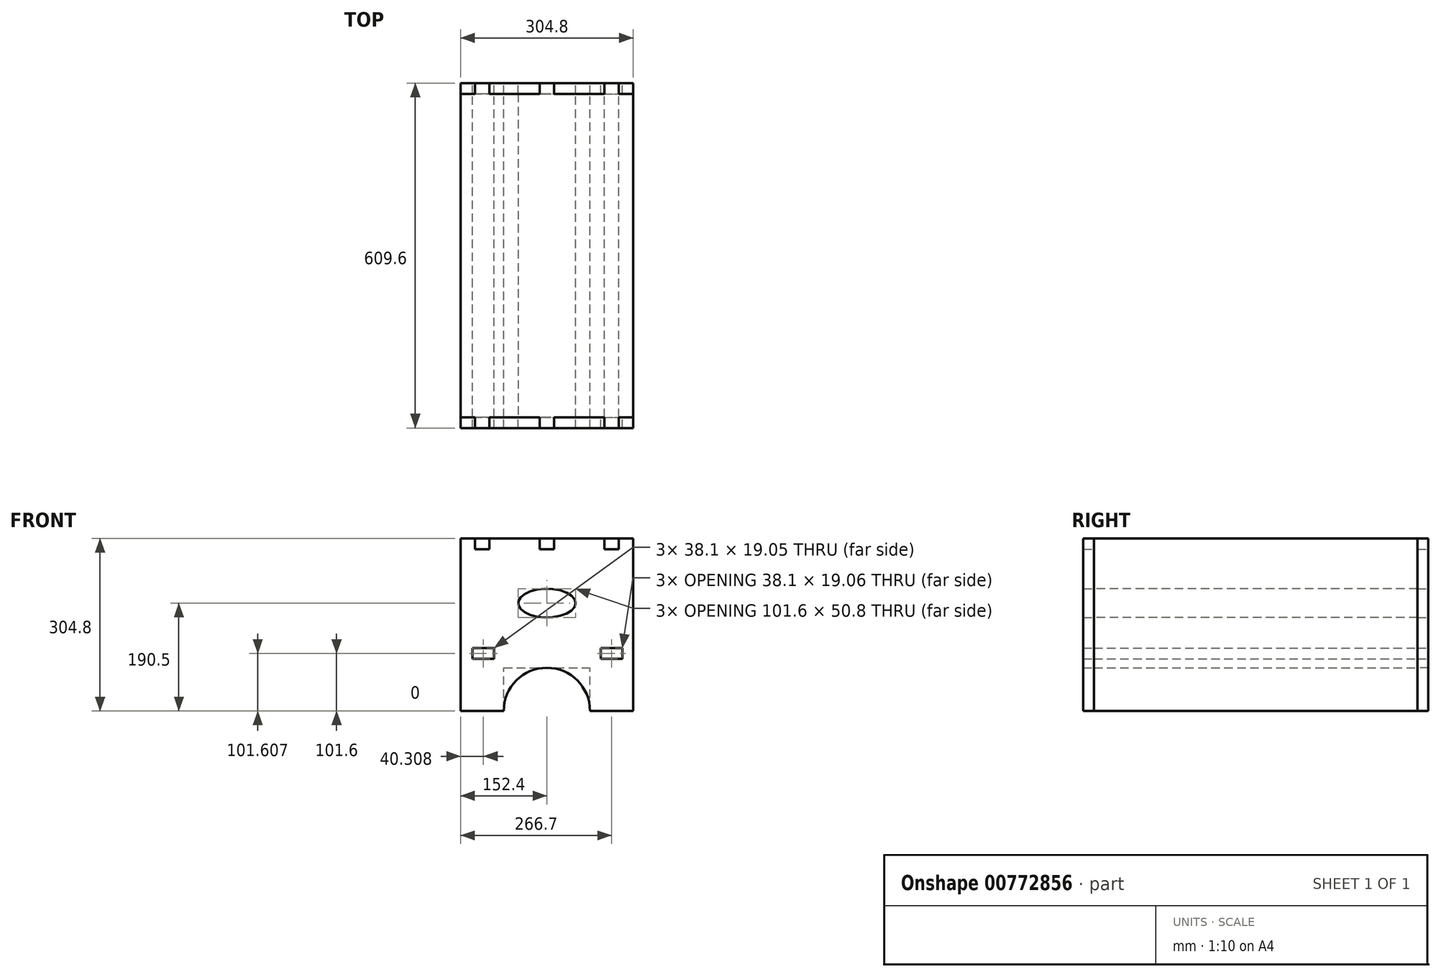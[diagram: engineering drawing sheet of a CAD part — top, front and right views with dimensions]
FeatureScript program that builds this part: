
annotation { "Feature Type Name" : "Feature", "Feature Type Description" : "" }
export const myFeature = defineFeature(function(context is Context, id is Id, definition is map)
    precondition{}
    {
        {
            var Q0;
            Q0=qCreatedBy(makeId("Front.planeOp"),FACE);
            var sketch = newSketch(context, id + "F0", { "sketchPlane" : qUnion([Q0])});
            skLineSegment(sketch, "E0.bottom", {"start": v(0, 0) * mm, "end": v(304.8, 0) * mm});
            skLineSegment(sketch, "E0.left", {"start": v(0, 0) * mm, "end": v(0, 304.8) * mm});
            skLineSegment(sketch, "E0.right", {"start": v(304.8, 0) * mm, "end": v(304.8, 304.8) * mm});
            skLineSegment(sketch, "E1", {"start": v(0, 0) * mm, "end": v(76.2, 0) * mm});
            skLineSegment(sketch, "E2", {"start": v(304.8, 0) * mm, "end": v(228.6, 0) * mm});
            skLineSegment(sketch, "E3", {"start": v(228.6, 0) * mm, "end": v(228.6, 76.2) * mm});
            skLineSegment(sketch, "E4", {"start": v(76.2, 0) * mm, "end": v(76.2, 76.2) * mm});
            skLineSegment(sketch, "E5", {"start": v(76.2, 76.2) * mm, "end": v(228.6, 76.2) * mm});
            skEllipse(sketch, "E6", {"center": v(152.4, 190.5) * mm, "majorRadius": 50.8 * mm, "minorRadius": 25.4 * mm, "majorAxis": v(1, 0)});
            skLineSegment(sketch, "E7.bottom", {"start": v(254, 111.13) * mm, "end": v(279.4, 111.13) * mm});
            skLineSegment(sketch, "E7.top", {"start": v(254, 92.07) * mm, "end": v(279.4, 92.07) * mm});
            skLineSegment(sketch, "E8", {"start": v(279.4, 111.13) * mm, "end": v(279.4, 92.07) * mm});
            skLineSegment(sketch, "E9", {"start": v(254, 111.13) * mm, "end": v(254, 92.07) * mm});
            skLineSegment(sketch, "E10.top", {"start": v(53, 92.08) * mm, "end": v(25.4, 92.08) * mm});
            skLineSegment(sketch, "E11.top", {"start": v(139.7, 285.75) * mm, "end": v(165.1, 285.75) * mm});
            skLineSegment(sketch, "E11.left", {"start": v(139.7, 304.8) * mm, "end": v(139.7, 285.75) * mm});
            skLineSegment(sketch, "E11.right", {"start": v(165.1, 304.8) * mm, "end": v(165.1, 285.75) * mm});
            skLineSegment(sketch, "E12", {"start": v(0, 304.8) * mm, "end": v(304.8, 304.8) * mm});
            skLineSegment(sketch, "E13", {"start": v(254, 304.8) * mm, "end": v(254, 285.75) * mm});
            skLineSegment(sketch, "E14", {"start": v(254, 285.75) * mm, "end": v(279.4, 285.75) * mm});
            skLineSegment(sketch, "E15", {"start": v(50.8, 304.8) * mm, "end": v(50.8, 285.75) * mm});
            skLineSegment(sketch, "E16", {"start": v(50.8, 285.75) * mm, "end": v(25.4, 285.75) * mm});
            skLineSegment(sketch, "E17", {"start": v(279.4, 285.75) * mm, "end": v(279.4, 304.8) * mm});
            skLineSegment(sketch, "E18", {"start": v(25.4, 285.75) * mm, "end": v(25.4, 304.8) * mm});
            skLineSegment(sketch, "E19.bottom", {"start": v(27.6, 111.13) * mm, "end": v(53, 111.13) * mm});
            skLineSegment(sketch, "E19.left", {"start": v(27.6, 111.13) * mm, "end": v(27.6, 92.08) * mm});
            skLineSegment(sketch, "E19.right", {"start": v(53, 111.13) * mm, "end": v(53, 92.08) * mm});
            skLineSegment(sketch, "E20", {"start": v(53, 92.08) * mm, "end": v(59.36, 92.08) * mm});
            skLineSegment(sketch, "E21.bottom", {"start": v(59.36, 92.08) * mm, "end": v(21.26, 92.08) * mm});
            skLineSegment(sketch, "E21.top", {"start": v(59.36, 111.13) * mm, "end": v(21.26, 111.13) * mm});
            skLineSegment(sketch, "E21.left", {"start": v(59.36, 92.08) * mm, "end": v(59.36, 111.13) * mm});
            skLineSegment(sketch, "E21.right", {"start": v(21.26, 92.08) * mm, "end": v(21.26, 111.13) * mm});
            skLineSegment(sketch, "E22", {"start": v(254, 92.07) * mm, "end": v(247.65, 92.07) * mm});
            skLineSegment(sketch, "E23.bottom", {"start": v(247.65, 92.07) * mm, "end": v(285.75, 92.07) * mm});
            skLineSegment(sketch, "E23.top", {"start": v(247.65, 111.12) * mm, "end": v(285.75, 111.12) * mm});
            skLineSegment(sketch, "E23.left", {"start": v(247.65, 92.07) * mm, "end": v(247.65, 111.12) * mm});
            skLineSegment(sketch, "E23.right", {"start": v(285.75, 92.07) * mm, "end": v(285.75, 111.12) * mm});
            skSolve(sketch);
        }
        {
            var Q0;
            {var subQ7=sQuery(id+"F0.wireOp",EDGE,"E0.left");Q0=makeQuery(id+"F0.imprint","IMPRINT",FACE,{"disambiguationData":[TD([[makeQuery(id+"F0.imprint","IMPRINT",EDGE,{"derivedFrom":subQ7}),-1.0]])]});}
            extrude(context, id + "F1", {"entities" : qUnion([Q0]), "depth" : 19.05 * mm, "offsetDistance" : 25.4 * mm});
        }
        {
            var Q0;
            Q0=makeQuery(id+"F1.opExtrude","CAP_FACE",FACE,{"disambiguationData":[OSD([sQuery(id+"F0.wireOp",EDGE,"E0.left"),sQuery(id+"F0.wireOp",EDGE,"E0.right"),sQuery(id+"F0.wireOp",EDGE,"E1"),sQuery(id+"F0.wireOp",EDGE,"E2"),sQuery(id+"F0.wireOp",EDGE,"E3"),sQuery(id+"F0.wireOp",EDGE,"E4"),sQuery(id+"F0.wireOp",EDGE,"E5"),sQuery(id+"F0.wireOp",EDGE,"E6"),sQuery(id+"F0.wireOp",EDGE,"E7.bottom"),sQuery(id+"F0.wireOp",EDGE,"E8"),sQuery(id+"F0.wireOp",EDGE,"E9"),sQuery(id+"F0.wireOp",EDGE,"E11.top"),sQuery(id+"F0.wireOp",EDGE,"E11.left"),sQuery(id+"F0.wireOp",EDGE,"E11.right"),sQuery(id+"F0.wireOp",EDGE,"E12"),sQuery(id+"F0.wireOp",EDGE,"E13"),sQuery(id+"F0.wireOp",EDGE,"E14"),sQuery(id+"F0.wireOp",EDGE,"E15"),sQuery(id+"F0.wireOp",EDGE,"E16"),sQuery(id+"F0.wireOp",EDGE,"E17"),sQuery(id+"F0.wireOp",EDGE,"E18"),sQuery(id+"F0.wireOp",EDGE,"E21.bottom"),sQuery(id+"F0.wireOp",EDGE,"E21.top"),sQuery(id+"F0.wireOp",EDGE,"E21.left"),sQuery(id+"F0.wireOp",EDGE,"E21.right"),sQuery(id+"F0.wireOp",EDGE,"E23.bottom"),sQuery(id+"F0.wireOp",EDGE,"E23.top"),sQuery(id+"F0.wireOp",EDGE,"E23.left"),sQuery(id+"F0.wireOp",EDGE,"E23.right")])],"isStart":true});
            var sketch = newSketch(context, id + "F2", { "sketchPlane" : qUnion([Q0])});
            skLineSegment(sketch, "E24.bottom", {"start": v(-247.65, 111.12) * mm, "end": v(-285.75, 111.12) * mm});
            skLineSegment(sketch, "E24.top", {"start": v(-247.65, 92.07) * mm, "end": v(-285.75, 92.07) * mm});
            skLineSegment(sketch, "E24.left", {"start": v(-247.65, 111.12) * mm, "end": v(-247.65, 92.07) * mm});
            skLineSegment(sketch, "E24.right", {"start": v(-285.75, 111.12) * mm, "end": v(-285.75, 92.07) * mm});
            skLineSegment(sketch, "E25.bottom", {"start": v(-59.36, 92.08) * mm, "end": v(-21.26, 92.08) * mm});
            skLineSegment(sketch, "E25.top", {"start": v(-59.36, 111.13) * mm, "end": v(-21.26, 111.13) * mm});
            skLineSegment(sketch, "E25.left", {"start": v(-59.36, 92.08) * mm, "end": v(-59.36, 111.13) * mm});
            skLineSegment(sketch, "E25.right", {"start": v(-21.26, 92.08) * mm, "end": v(-21.26, 111.13) * mm});
            skLineSegment(sketch, "E26.bottom", {"start": v(-25.4, 285.75) * mm, "end": v(-50.8, 285.75) * mm});
            skLineSegment(sketch, "E26.top", {"start": v(-25.4, 304.8) * mm, "end": v(-50.8, 304.8) * mm});
            skLineSegment(sketch, "E26.left", {"start": v(-25.4, 285.75) * mm, "end": v(-25.4, 304.8) * mm});
            skLineSegment(sketch, "E26.right", {"start": v(-50.8, 285.75) * mm, "end": v(-50.8, 304.8) * mm});
            skLineSegment(sketch, "E27.bottom", {"start": v(-139.7, 285.75) * mm, "end": v(-165.1, 285.75) * mm});
            skLineSegment(sketch, "E27.top", {"start": v(-139.7, 304.8) * mm, "end": v(-165.1, 304.8) * mm});
            skLineSegment(sketch, "E27.left", {"start": v(-139.7, 285.75) * mm, "end": v(-139.7, 304.8) * mm});
            skLineSegment(sketch, "E27.right", {"start": v(-165.1, 285.75) * mm, "end": v(-165.1, 304.8) * mm});
            skLineSegment(sketch, "E28.bottom", {"start": v(-254, 285.75) * mm, "end": v(-279.4, 285.75) * mm});
            skLineSegment(sketch, "E28.top", {"start": v(-254, 304.8) * mm, "end": v(-279.4, 304.8) * mm});
            skLineSegment(sketch, "E28.left", {"start": v(-254, 285.75) * mm, "end": v(-254, 304.8) * mm});
            skLineSegment(sketch, "E28.right", {"start": v(-279.4, 285.75) * mm, "end": v(-279.4, 304.8) * mm});
            skLineSegment(sketch, "E29", {"start": v(-304.8, 304.8) * mm, "end": v(-304.8, 285.75) * mm});
            skLineSegment(sketch, "E30", {"start": v(-304.8, 285.75) * mm, "end": v(0, 285.75) * mm});
            skSolve(sketch);
        }
        {
            var Q0;
            {var subQ0=sQuery(id+"F2.wireOp",EDGE,"E28.right");Q0=makeQuery(id+"F2.imprint","IMPRINT",FACE,{"disambiguationData":[TD([[makeQuery(id+"F2.imprint","IMPRINT",EDGE,{"derivedFrom":subQ0}),1.0]])]});}
            var Q1;
            Q1=makeQuery(id+"F2.imprint","IMPRINT",FACE,{"disambiguationData":[TD([[makeQuery(id+"F2.imprint","IMPRINT",EDGE,{"derivedFrom":sQuery(id+"F2.wireOp",EDGE,"E28.top")}),1.0]])]});
            var Q2;
            {var subQ0=sQuery(id+"F2.wireOp",EDGE,"E27.right");Q2=makeQuery(id+"F2.imprint","IMPRINT",FACE,{"disambiguationData":[TD([[makeQuery(id+"F2.imprint","IMPRINT",EDGE,{"derivedFrom":subQ0}),-1.0]])]});}
            var Q3;
            Q3=makeQuery(id+"F2.imprint","IMPRINT",FACE,{"disambiguationData":[TD([[makeQuery(id+"F2.imprint","IMPRINT",EDGE,{"derivedFrom":sQuery(id+"F2.wireOp",EDGE,"E27.top")}),1.0]])]});
            var Q4;
            {var subQ0=sQuery(id+"F2.wireOp",EDGE,"E26.right");Q4=makeQuery(id+"F2.imprint","IMPRINT",FACE,{"disambiguationData":[TD([[makeQuery(id+"F2.imprint","IMPRINT",EDGE,{"derivedFrom":subQ0}),-1.0]])]});}
            var Q5;
            Q5=makeQuery(id+"F2.imprint","IMPRINT",FACE,{"disambiguationData":[TD([[makeQuery(id+"F2.imprint","IMPRINT",EDGE,{"derivedFrom":sQuery(id+"F2.wireOp",EDGE,"E26.top")}),1.0]])]});
            var Q6;
            {var subQ0=sQuery(id+"F2.wireOp",EDGE,"E26.left");Q6=makeQuery(id+"F2.imprint","IMPRINT",FACE,{"disambiguationData":[TD([[makeQuery(id+"F2.imprint","IMPRINT",EDGE,{"derivedFrom":subQ0}),-1.0]])]});}
            var Q7;
            Q7=makeQuery(id+"F2.imprint","IMPRINT",FACE,{"disambiguationData":[TD([[makeQuery(id+"F2.imprint","IMPRINT",EDGE,{"derivedFrom":sQuery(id+"F2.wireOp",EDGE,"E25.bottom")}),1.0]])]});
            var Q8;
            Q8=makeQuery(id+"F2.imprint","IMPRINT",FACE,{"disambiguationData":[TD([[makeQuery(id+"F2.imprint","IMPRINT",EDGE,{"derivedFrom":sQuery(id+"F2.wireOp",EDGE,"E24.top")}),-1.0]])]});
            extrude(context, id + "F3", {"entities" : qUnion([Q0, Q1, Q2, Q3, Q4, Q5, Q6, Q7, Q8]), "oppositeDirection" : true, "depth" : 609.6 * mm, "offsetDistance" : 25.4 * mm});
        }
        {
            var Q0;
            Q0=makeQuery(id+"F1.opExtrude","SWEPT_BODY",BODY,{"disambiguationData":[OSD([sQuery(id+"F0.wireOp",EDGE,"E0.left"),sQuery(id+"F0.wireOp",EDGE,"E0.right"),sQuery(id+"F0.wireOp",EDGE,"E1"),sQuery(id+"F0.wireOp",EDGE,"E2"),sQuery(id+"F0.wireOp",EDGE,"E3"),sQuery(id+"F0.wireOp",EDGE,"E4"),sQuery(id+"F0.wireOp",EDGE,"E5"),sQuery(id+"F0.wireOp",EDGE,"E6"),sQuery(id+"F0.wireOp",EDGE,"E7.bottom"),sQuery(id+"F0.wireOp",EDGE,"E8"),sQuery(id+"F0.wireOp",EDGE,"E9"),sQuery(id+"F0.wireOp",EDGE,"E11.top"),sQuery(id+"F0.wireOp",EDGE,"E11.left"),sQuery(id+"F0.wireOp",EDGE,"E11.right"),sQuery(id+"F0.wireOp",EDGE,"E12"),sQuery(id+"F0.wireOp",EDGE,"E13"),sQuery(id+"F0.wireOp",EDGE,"E14"),sQuery(id+"F0.wireOp",EDGE,"E15"),sQuery(id+"F0.wireOp",EDGE,"E16"),sQuery(id+"F0.wireOp",EDGE,"E17"),sQuery(id+"F0.wireOp",EDGE,"E18"),sQuery(id+"F0.wireOp",EDGE,"E21.bottom"),sQuery(id+"F0.wireOp",EDGE,"E21.top"),sQuery(id+"F0.wireOp",EDGE,"E21.left"),sQuery(id+"F0.wireOp",EDGE,"E21.right"),sQuery(id+"F0.wireOp",EDGE,"E23.bottom"),sQuery(id+"F0.wireOp",EDGE,"E23.top"),sQuery(id+"F0.wireOp",EDGE,"E23.left"),sQuery(id+"F0.wireOp",EDGE,"E23.right")])]});
            var Q1;
            Q1=makeQuery(id+"F1.opExtrude","CAP_FACE",FACE,{"disambiguationData":[OSD([sQuery(id+"F0.wireOp",EDGE,"E0.left"),sQuery(id+"F0.wireOp",EDGE,"E0.right"),sQuery(id+"F0.wireOp",EDGE,"E1"),sQuery(id+"F0.wireOp",EDGE,"E2"),sQuery(id+"F0.wireOp",EDGE,"E3"),sQuery(id+"F0.wireOp",EDGE,"E4"),sQuery(id+"F0.wireOp",EDGE,"E5"),sQuery(id+"F0.wireOp",EDGE,"E6"),sQuery(id+"F0.wireOp",EDGE,"E7.bottom"),sQuery(id+"F0.wireOp",EDGE,"E8"),sQuery(id+"F0.wireOp",EDGE,"E9"),sQuery(id+"F0.wireOp",EDGE,"E11.top"),sQuery(id+"F0.wireOp",EDGE,"E11.left"),sQuery(id+"F0.wireOp",EDGE,"E11.right"),sQuery(id+"F0.wireOp",EDGE,"E12"),sQuery(id+"F0.wireOp",EDGE,"E13"),sQuery(id+"F0.wireOp",EDGE,"E14"),sQuery(id+"F0.wireOp",EDGE,"E15"),sQuery(id+"F0.wireOp",EDGE,"E16"),sQuery(id+"F0.wireOp",EDGE,"E17"),sQuery(id+"F0.wireOp",EDGE,"E18"),sQuery(id+"F0.wireOp",EDGE,"E21.bottom"),sQuery(id+"F0.wireOp",EDGE,"E21.top"),sQuery(id+"F0.wireOp",EDGE,"E21.left"),sQuery(id+"F0.wireOp",EDGE,"E21.right"),sQuery(id+"F0.wireOp",EDGE,"E23.bottom"),sQuery(id+"F0.wireOp",EDGE,"E23.top"),sQuery(id+"F0.wireOp",EDGE,"E23.left"),sQuery(id+"F0.wireOp",EDGE,"E23.right")])],"isStart":false});
            transform(context, id + "F4", {"entities" : qUnion([Q0]), "transformType" : TransformType.TRANSLATION_DISTANCE, "transformDirection" : qUnion([Q1]), "distance" : 590.55 * mm, "makeCopy" : true});
        }
        {
            var Q0;
            Q0=makeQuery(id+"F1.opExtrude","SWEPT_EDGE",EDGE,{"disambiguationData":[OSD([sQuery(id+"F0.wireOp",EDGE,"E4"),sQuery(id+"F0.wireOp",EDGE,"E5")])]});
            var Q1;
            Q1=makeQuery(id+"F1.opExtrude","SWEPT_EDGE",EDGE,{"disambiguationData":[OSD([sQuery(id+"F0.wireOp",EDGE,"E3"),sQuery(id+"F0.wireOp",EDGE,"E5")])]});
            var Q2;
            Q2=makeQuery(id+"F4.opPattern","COPY",EDGE,{"derivedFrom":makeQuery(id+"F1.opExtrude","SWEPT_EDGE",EDGE,{"disambiguationData":[OSD([sQuery(id+"F0.wireOp",EDGE,"E3"),sQuery(id+"F0.wireOp",EDGE,"E5")])]}),"instanceName":"1"});
            var Q3;
            Q3=makeQuery(id+"F4.opPattern","COPY",EDGE,{"derivedFrom":makeQuery(id+"F1.opExtrude","SWEPT_EDGE",EDGE,{"disambiguationData":[OSD([sQuery(id+"F0.wireOp",EDGE,"E4"),sQuery(id+"F0.wireOp",EDGE,"E5")])]}),"instanceName":"1"});
            fillet(context, id + "F5", {"entities" : qUnion([Q0, Q1, Q2, Q3]), "radius" : 76.2 * mm, "tangentPropagation" : true, "allowEdgeOverflow" : false});
        }
        {
            var Q0;
            Q0=makeQuery(id+"F4.opPattern","COPY",BODY,{"derivedFrom":makeQuery(id+"F1.opExtrude","SWEPT_BODY",BODY,{"disambiguationData":[OSD([sQuery(id+"F0.wireOp",EDGE,"E0.left"),sQuery(id+"F0.wireOp",EDGE,"E0.right"),sQuery(id+"F0.wireOp",EDGE,"E1"),sQuery(id+"F0.wireOp",EDGE,"E2"),sQuery(id+"F0.wireOp",EDGE,"E3"),sQuery(id+"F0.wireOp",EDGE,"E4"),sQuery(id+"F0.wireOp",EDGE,"E5"),sQuery(id+"F0.wireOp",EDGE,"E6"),sQuery(id+"F0.wireOp",EDGE,"E7.bottom"),sQuery(id+"F0.wireOp",EDGE,"E8"),sQuery(id+"F0.wireOp",EDGE,"E9"),sQuery(id+"F0.wireOp",EDGE,"E11.top"),sQuery(id+"F0.wireOp",EDGE,"E11.left"),sQuery(id+"F0.wireOp",EDGE,"E11.right"),sQuery(id+"F0.wireOp",EDGE,"E12"),sQuery(id+"F0.wireOp",EDGE,"E13"),sQuery(id+"F0.wireOp",EDGE,"E14"),sQuery(id+"F0.wireOp",EDGE,"E15"),sQuery(id+"F0.wireOp",EDGE,"E16"),sQuery(id+"F0.wireOp",EDGE,"E17"),sQuery(id+"F0.wireOp",EDGE,"E18"),sQuery(id+"F0.wireOp",EDGE,"E21.bottom"),sQuery(id+"F0.wireOp",EDGE,"E21.top"),sQuery(id+"F0.wireOp",EDGE,"E21.left"),sQuery(id+"F0.wireOp",EDGE,"E21.right"),sQuery(id+"F0.wireOp",EDGE,"E23.bottom"),sQuery(id+"F0.wireOp",EDGE,"E23.top"),sQuery(id+"F0.wireOp",EDGE,"E23.left"),sQuery(id+"F0.wireOp",EDGE,"E23.right")])]}),"instanceName":"1"});
            var Q1;
            Q1=makeQuery(id+"F3.opExtrude","SWEPT_BODY",BODY,{"disambiguationData":[OSD([sQuery(id+"F0.wireOp",EDGE,"E0.left"),sQuery(id+"F0.wireOp",EDGE,"E12"),sQuery(id+"F2.wireOp",EDGE,"E26.top"),sQuery(id+"F2.wireOp",EDGE,"E27.top"),sQuery(id+"F2.wireOp",EDGE,"E28.top"),sQuery(id+"F2.wireOp",EDGE,"E29"),sQuery(id+"F2.wireOp",EDGE,"E30")])]});
            booleanBodies(context, id + "F6", {"operationType" : BooleanOperationType.SUBTRACTION, "tools" : qUnion([Q0]), "targets" : qUnion([Q1]), "keepTools" : true});
        }
        {
            var Q0;
            Q0=makeQuery(id+"F1.opExtrude","SWEPT_BODY",BODY,{"disambiguationData":[OSD([sQuery(id+"F0.wireOp",EDGE,"E0.left"),sQuery(id+"F0.wireOp",EDGE,"E0.right"),sQuery(id+"F0.wireOp",EDGE,"E1"),sQuery(id+"F0.wireOp",EDGE,"E2"),sQuery(id+"F0.wireOp",EDGE,"E3"),sQuery(id+"F0.wireOp",EDGE,"E4"),sQuery(id+"F0.wireOp",EDGE,"E5"),sQuery(id+"F0.wireOp",EDGE,"E6"),sQuery(id+"F0.wireOp",EDGE,"E7.bottom"),sQuery(id+"F0.wireOp",EDGE,"E8"),sQuery(id+"F0.wireOp",EDGE,"E9"),sQuery(id+"F0.wireOp",EDGE,"E11.top"),sQuery(id+"F0.wireOp",EDGE,"E11.left"),sQuery(id+"F0.wireOp",EDGE,"E11.right"),sQuery(id+"F0.wireOp",EDGE,"E12"),sQuery(id+"F0.wireOp",EDGE,"E13"),sQuery(id+"F0.wireOp",EDGE,"E14"),sQuery(id+"F0.wireOp",EDGE,"E15"),sQuery(id+"F0.wireOp",EDGE,"E16"),sQuery(id+"F0.wireOp",EDGE,"E17"),sQuery(id+"F0.wireOp",EDGE,"E18"),sQuery(id+"F0.wireOp",EDGE,"E21.bottom"),sQuery(id+"F0.wireOp",EDGE,"E21.top"),sQuery(id+"F0.wireOp",EDGE,"E21.left"),sQuery(id+"F0.wireOp",EDGE,"E21.right"),sQuery(id+"F0.wireOp",EDGE,"E23.bottom"),sQuery(id+"F0.wireOp",EDGE,"E23.top"),sQuery(id+"F0.wireOp",EDGE,"E23.left"),sQuery(id+"F0.wireOp",EDGE,"E23.right")])]});
            var Q1;
            Q1=makeQuery(id+"F3.opExtrude","SWEPT_BODY",BODY,{"disambiguationData":[OSD([sQuery(id+"F0.wireOp",EDGE,"E0.left"),sQuery(id+"F0.wireOp",EDGE,"E12"),sQuery(id+"F2.wireOp",EDGE,"E26.top"),sQuery(id+"F2.wireOp",EDGE,"E27.top"),sQuery(id+"F2.wireOp",EDGE,"E28.top"),sQuery(id+"F2.wireOp",EDGE,"E29"),sQuery(id+"F2.wireOp",EDGE,"E30")])]});
            booleanBodies(context, id + "F7", {"operationType" : BooleanOperationType.SUBTRACTION, "tools" : qUnion([Q0]), "targets" : qUnion([Q1]), "keepTools" : true});
        }
    });
